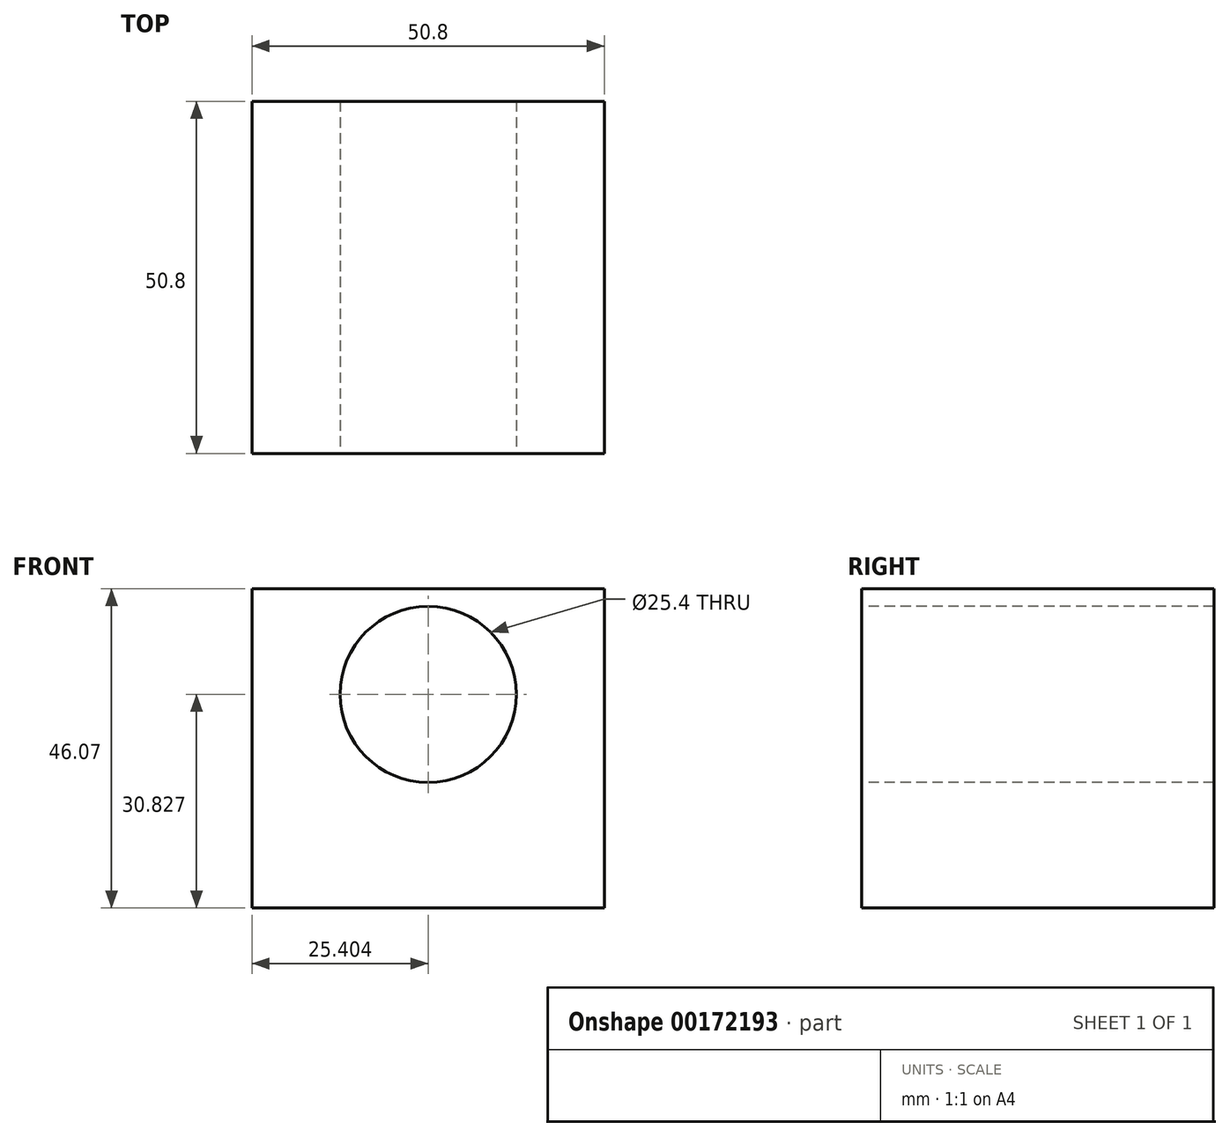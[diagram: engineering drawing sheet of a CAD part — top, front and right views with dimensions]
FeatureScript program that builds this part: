
annotation { "Feature Type Name" : "Feature", "Feature Type Description" : "" }
export const myFeature = defineFeature(function(context is Context, id is Id, definition is map)
    precondition{}
    {
        {
            var Q0;
            Q0=qCreatedBy(makeId("Front.planeOp"),FACE);
            var sketch = newSketch(context, id + "F0", { "sketchPlane" : qUnion([Q0])});
            skLineSegment(sketch, "E0.bottom", {"start": v(-56.86, 32.23) * mm, "end": v(-6.06, 32.23) * mm});
            skLineSegment(sketch, "E0.top", {"start": v(-56.86, -13.84) * mm, "end": v(-6.06, -13.84) * mm});
            skLineSegment(sketch, "E0.left", {"start": v(-56.86, 32.23) * mm, "end": v(-56.86, -13.84) * mm});
            skLineSegment(sketch, "E0.right", {"start": v(-6.06, 32.23) * mm, "end": v(-6.06, -13.84) * mm});
            skSolve(sketch);
        }
        {
            var Q0;
            Q0 = qSketchRegion(id + "F0", true);
            extrude(context, id + "F1", {"entities" : qUnion([Q0]), "depth" : 50.8 * mm});
        }
        {
            var Q0;
            Q0=makeQuery(id+"F1.opExtrude","CAP_FACE",FACE,{"disambiguationData":[OSD([sQuery(id+"F0.wireOp",EDGE,"E0.bottom"),sQuery(id+"F0.wireOp",EDGE,"E0.top"),sQuery(id+"F0.wireOp",EDGE,"E0.left"),sQuery(id+"F0.wireOp",EDGE,"E0.right")])],"isStart":false});
            var sketch = newSketch(context, id + "F2", { "sketchPlane" : qUnion([Q0])});
            skCircle(sketch, "E1", {"center": v(-31.46, 16.99) * mm, "radius": 12.7 * mm});
            skPoint(sketch, "E1.centerSnap0", {"position": v(-31.46, 32.23) * mm});
            skSolve(sketch);
        }
        {
            var Q0;
            Q0=sQuery(id+"F2.wireOp",VERTEX,"E1.center");
            var Q1;
            Q1=makeQuery(id+"F1.opExtrude","SWEPT_BODY",BODY,{"disambiguationData":[OSD([sQuery(id+"F0.wireOp",EDGE,"E0.bottom"),sQuery(id+"F0.wireOp",EDGE,"E0.top"),sQuery(id+"F0.wireOp",EDGE,"E0.left"),sQuery(id+"F0.wireOp",EDGE,"E0.right")])]});
            hole(context, id + "F3", {"style" : HoleStyle.SIMPLE, "endStyle" : HoleEndStyle.THROUGH, "holeDiameter" : 25.4 * mm, "locations" : qUnion([Q0]), "scope" : qUnion([Q1]), "isTappedThrough" : true});
        }
    });
